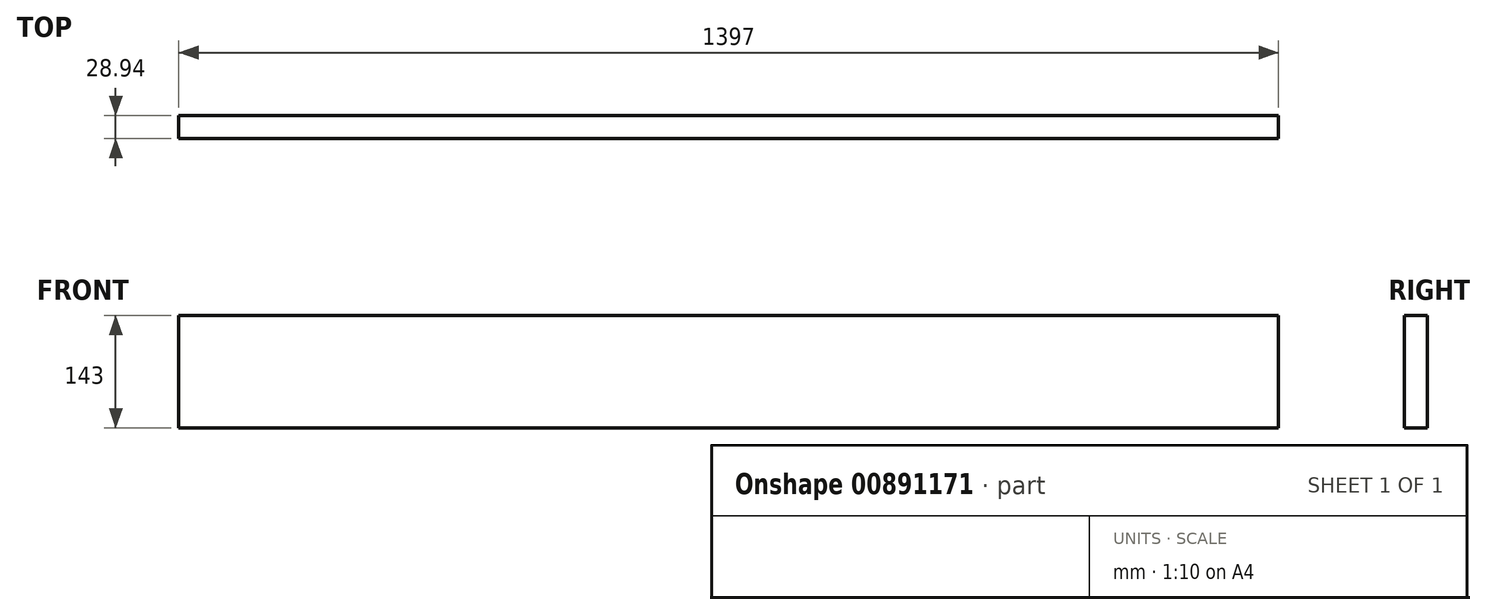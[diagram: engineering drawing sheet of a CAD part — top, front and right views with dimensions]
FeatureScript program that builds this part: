
annotation { "Feature Type Name" : "Feature", "Feature Type Description" : "" }
export const myFeature = defineFeature(function(context is Context, id is Id, definition is map)
    precondition{}
    {
        {
            var Q0;
            Q0=qCreatedBy(makeId("Top.planeOp"),FACE);
            var sketch = newSketch(context, id + "F0", { "sketchPlane" : qUnion([Q0])});
            skLineSegment(sketch, "E0.bottom", {"start": v(1254.3, -60.49) * mm, "end": v(-142.7, -60.49) * mm});
            skLineSegment(sketch, "E0.top", {"start": v(1254.3, -31.55) * mm, "end": v(-142.7, -31.55) * mm});
            skLineSegment(sketch, "E0.left", {"start": v(1254.3, -60.49) * mm, "end": v(1254.3, -31.55) * mm});
            skLineSegment(sketch, "E0.right", {"start": v(-142.7, -60.49) * mm, "end": v(-142.7, -31.55) * mm});
            skSolve(sketch);
        }
        {
            var Q0;
            Q0 = qSketchRegion(id + "F0", true);
            extrude(context, id + "F1", {"entities" : qUnion([Q0]), "depth" : 143 * mm, "offsetDistance" : 25.4 * mm});
        }
    });
